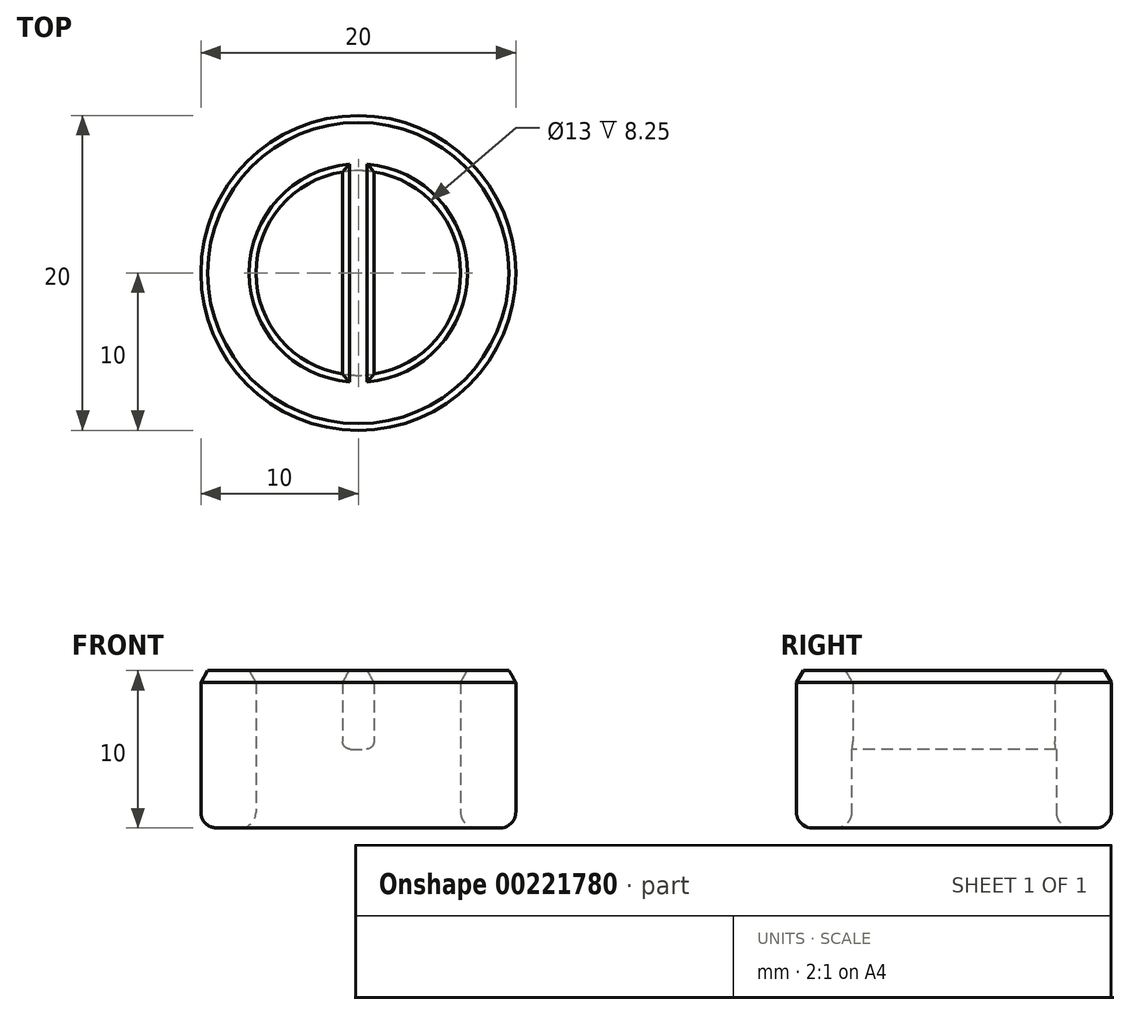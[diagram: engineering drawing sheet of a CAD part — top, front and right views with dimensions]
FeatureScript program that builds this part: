
annotation { "Feature Type Name" : "Feature", "Feature Type Description" : "" }
export const myFeature = defineFeature(function(context is Context, id is Id, definition is map)
    precondition{}
    {
        {
            var Q0;
            Q0=qCreatedBy(makeId("Top.planeOp"),FACE);
            var sketch = newSketch(context, id + "F0", { "sketchPlane" : qUnion([Q0])});
            skArc(sketch, "E0", {"start": v(-1, 6.42) * mm, "mid": v(-6.5, 0) * mm, "end": v(-1, -6.42) * mm});
            skCircle(sketch, "E1", {"center": v(0, 0) * mm, "radius": 10 * mm});
            skLineSegment(sketch, "E2", {"start": v(1, 6.42) * mm, "end": v(1, -6.42) * mm});
            skLineSegment(sketch, "E3", {"start": v(-1, 6.42) * mm, "end": v(-1, -6.42) * mm});
            skArc(sketch, "E4.trimOffspring", {"start": v(1, -6.42) * mm, "mid": v(6.5, 0) * mm, "end": v(1, 6.42) * mm});
            skSolve(sketch);
        }
        {
            var Q0;
            Q0 = qSketchRegion(id + "F0", true);
            extrude(context, id + "F1", {"entities" : qUnion([Q0]), "depth" : 5 * mm});
        }
        {
            var Q0;
            Q0=makeQuery(id+"F1.opExtrude","CAP_FACE",FACE,{"disambiguationData":[OSD([sQuery(id+"F0.wireOp",EDGE,"E0"),sQuery(id+"F0.wireOp",EDGE,"E1"),sQuery(id+"F0.wireOp",EDGE,"E2"),sQuery(id+"F0.wireOp",EDGE,"E3"),sQuery(id+"F0.wireOp",EDGE,"E4.trimOffspring")])],"isStart":true});
            var sketch = newSketch(context, id + "F2", { "sketchPlane" : qUnion([Q0])});
            skCircle(sketch, "E5", {"center": v(0, 0) * mm, "radius": 6.5 * mm});
            skCircle(sketch, "E6", {"center": v(0, 0) * mm, "radius": 10 * mm});
            skSolve(sketch);
        }
        {
            var Q0;
            Q0 = qSketchRegion(id + "F2", true);
            extrude(context, id + "F3", {"entities" : qUnion([Q0]), "operationType" : NewBodyOperationType.ADD, "depth" : 5 * mm});
        }
        {
            var Q0;
            Q0=makeQuery(id+"F1.opExtrude","CAP_EDGE",EDGE,{"disambiguationData":[OSD([sQuery(id+"F0.wireOp",EDGE,"E3")])],"isStart":true});
            var Q1;
            Q1=makeQuery(id+"F1.opExtrude","CAP_EDGE",EDGE,{"disambiguationData":[OSD([sQuery(id+"F0.wireOp",EDGE,"E2")])],"isStart":true});
            fillet(context, id + "F4", {"entities" : qUnion([Q0, Q1]), "radius" : .5 * mm, "tangentPropagation" : true, "allowEdgeOverflow" : false});
        }
        {
            var Q0;
            Q0=makeQuery(id+"F3.opExtrude","CAP_FACE",FACE,{"disambiguationData":[OSD([sQuery(id+"F2.wireOp",EDGE,"E5"),sQuery(id+"F2.wireOp",EDGE,"E6")])],"isStart":false});
            fillet(context, id + "F5", {"entities" : qUnion([Q0]), "radius" : 1 * mm, "tangentPropagation" : true, "allowEdgeOverflow" : false});
        }
        {
            var Q0;
            Q0=makeQuery(id+"F1.opExtrude","CAP_FACE",FACE,{"disambiguationData":[OSD([sQuery(id+"F0.wireOp",EDGE,"E0"),sQuery(id+"F0.wireOp",EDGE,"E1"),sQuery(id+"F0.wireOp",EDGE,"E2"),sQuery(id+"F0.wireOp",EDGE,"E3"),sQuery(id+"F0.wireOp",EDGE,"E4.trimOffspring")])],"isStart":false});
            chamfer(context, id + "F6", {"entities" : qUnion([Q0]), "chamferType" : ChamferType.OFFSET_ANGLE, "width" : .75 * mm, "oppositeDirection" : false, "angle" : 30 * degree, "tangentPropagation" : true});
        }
    });
